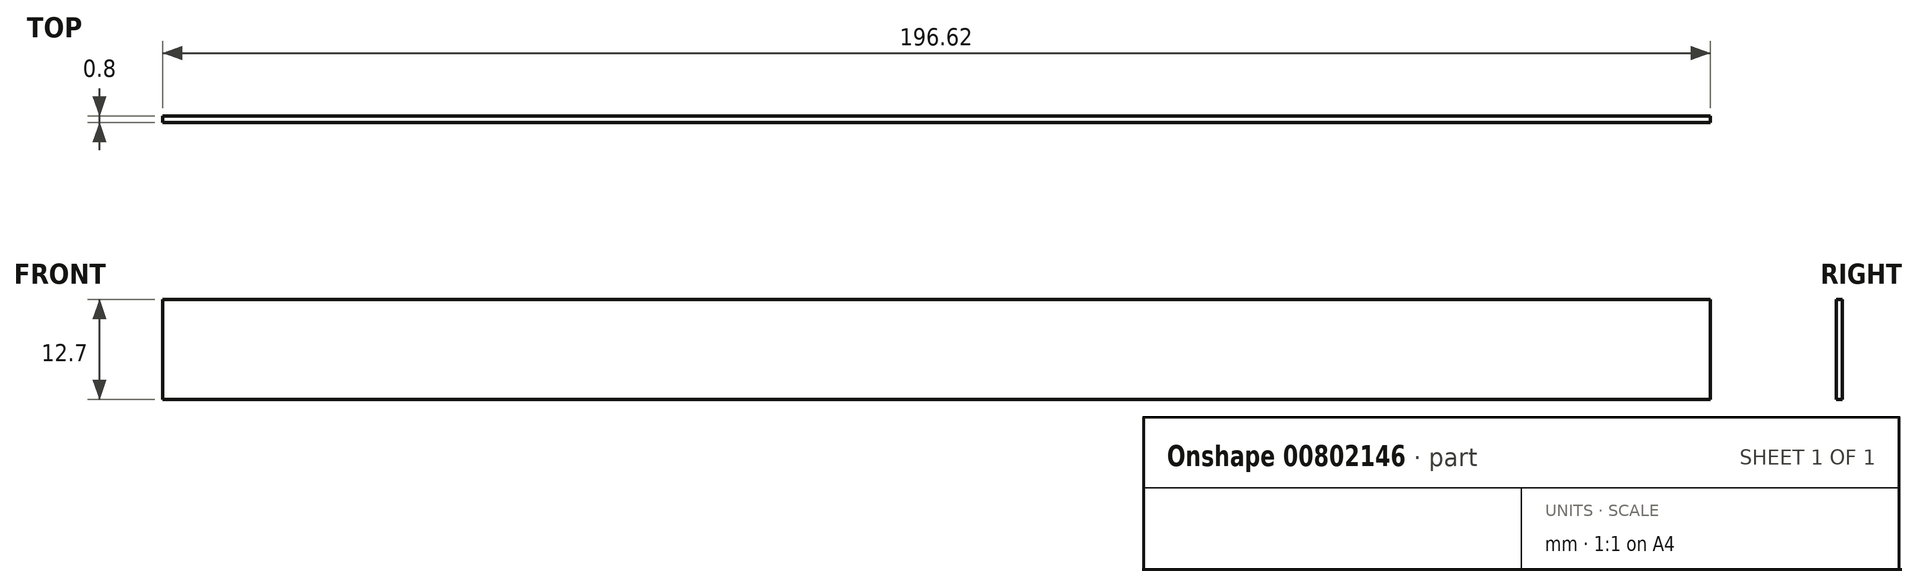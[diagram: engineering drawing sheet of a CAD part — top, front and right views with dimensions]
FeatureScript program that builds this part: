
annotation { "Feature Type Name" : "Feature", "Feature Type Description" : "" }
export const myFeature = defineFeature(function(context is Context, id is Id, definition is map)
    precondition{}
    {
        {
            var Q0;
            Q0=qCreatedBy(makeId("Right.planeOp"),FACE);
            var sketch = newSketch(context, id + "F0", { "sketchPlane" : qUnion([Q0])});
            skLineSegment(sketch, "E0.bottom", {"start": v(0, 0) * mm, "end": v(0.8, 0) * mm});
            skLineSegment(sketch, "E0.top", {"start": v(0, 12.7) * mm, "end": v(0.8, 12.7) * mm});
            skLineSegment(sketch, "E0.left", {"start": v(0, 0) * mm, "end": v(0, 12.7) * mm});
            skLineSegment(sketch, "E0.right", {"start": v(0.8, 0) * mm, "end": v(0.8, 12.7) * mm});
            skSolve(sketch);
        }
        {
            var Q0;
            Q0=qSketchRegion(id+"F0",true);
            extrude(context, id + "F1", {"entities" : qUnion([Q0]), "depth" : 196.62 * mm, "offsetDistance" : 25 * mm});
        }
    });
